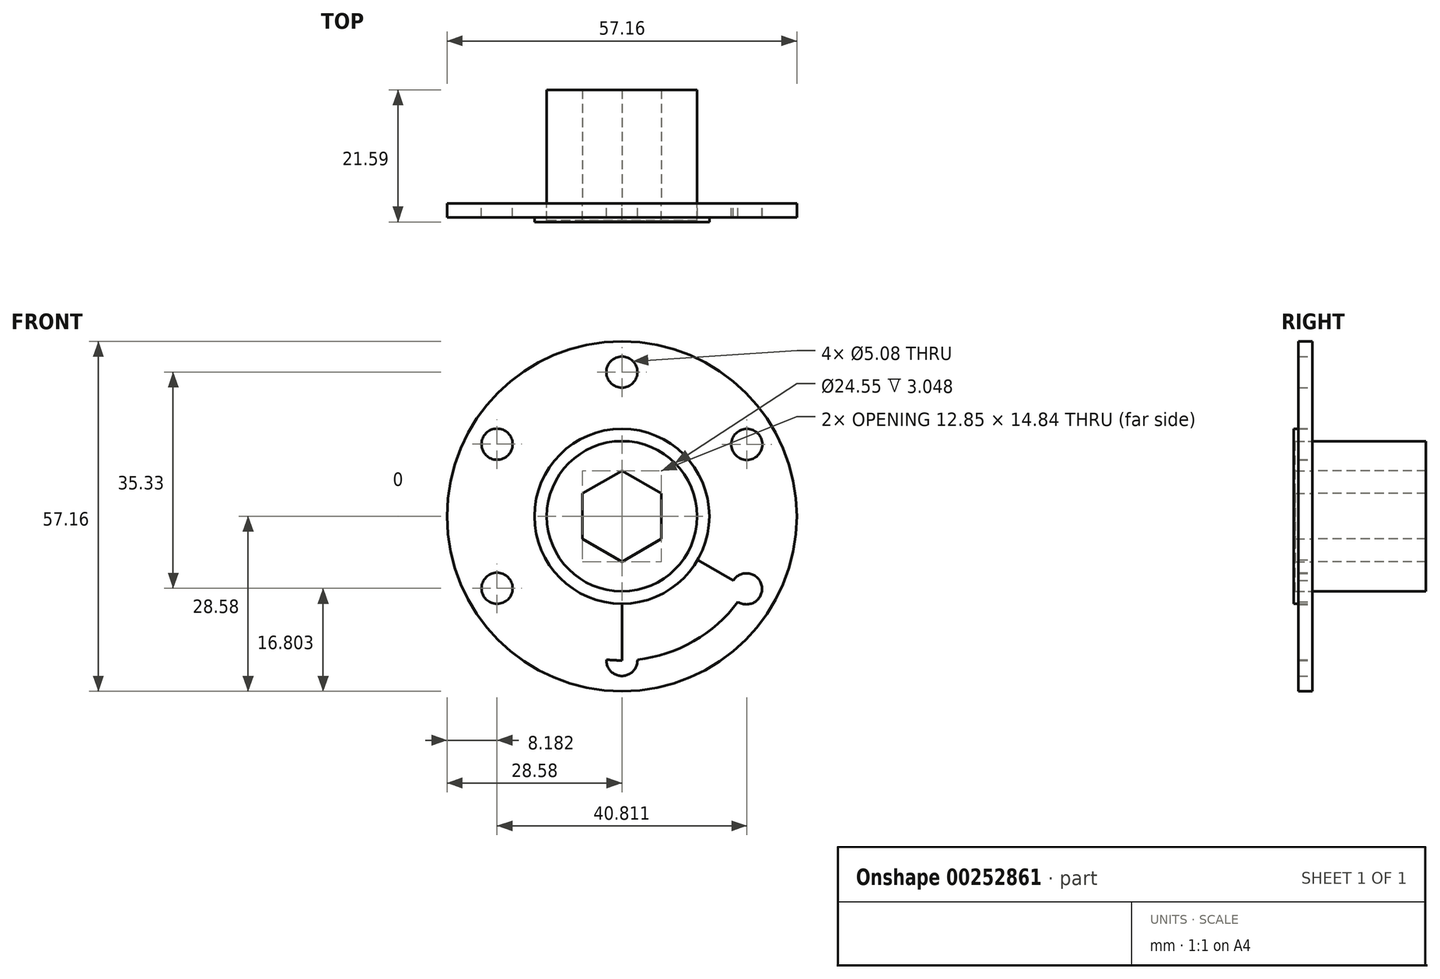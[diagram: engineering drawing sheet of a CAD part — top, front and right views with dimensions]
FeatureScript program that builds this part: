
annotation { "Feature Type Name" : "Feature", "Feature Type Description" : "" }
export const myFeature = defineFeature(function(context is Context, id is Id, definition is map)
    precondition{}
    {
        {
            var Q0;
            Q0=qCreatedBy(makeId("Front.planeOp"),FACE);
            var sketch = newSketch(context, id + "F0", { "sketchPlane" : qUnion([Q0])});
            skCircle(sketch, "E0", {"center": v(0, 0) * mm, "radius": 28.58 * mm});
            skPoint(sketch, "E1", {"position": v(0, 28.58) * mm});
            skPoint(sketch, "E2", {"position": v(0, -28.58) * mm});
            skLineSegment(sketch, "E3", {"start": v(0, 0) * mm, "end": v(-47.7, 27.54) * mm});
            skLineSegment(sketch, "E4.MirrorCS", {"start": v(0, 0) * mm, "end": v(-47.7, -27.54) * mm});
            skCircle(sketch, "E5.cCircle", {"center": v(0, 0) * mm, "radius": 6.43 * mm, "construction": true});
            skLineSegment(sketch, "E5.0", {"start": v(0, 7.42) * mm, "end": v(6.43, 3.71) * mm});
            skLineSegment(sketch, "E5.1", {"start": v(6.43, 3.71) * mm, "end": v(6.43, -3.71) * mm});
            skLineSegment(sketch, "E5.2", {"start": v(6.43, -3.71) * mm, "end": v(0, -7.42) * mm});
            skLineSegment(sketch, "E5.3", {"start": v(0, -7.42) * mm, "end": v(-6.43, -3.71) * mm});
            skLineSegment(sketch, "E5.4", {"start": v(-6.43, -3.71) * mm, "end": v(-6.43, 3.71) * mm});
            skLineSegment(sketch, "E5.5", {"start": v(-6.43, 3.71) * mm, "end": v(0, 7.42) * mm});
            skPoint(sketch, "E5.0.midPoint", {"position": v(3.21, 5.57) * mm});
            skCircle(sketch, "E6", {"center": v(0, 0) * mm, "radius": 23.55 * mm});
            skCircle(sketch, "E7", {"center": v(-20.4, 11.78) * mm, "radius": 2.54 * mm});
            skCircle(sketch, "E8", {"center": v(-20.4, -11.78) * mm, "radius": 2.54 * mm});
            skCircle(sketch, "E9", {"center": v(0, -23.55) * mm, "radius": 2.54 * mm});
            skCircle(sketch, "E10", {"center": v(0, 23.55) * mm, "radius": 2.54 * mm});
            skCircle(sketch, "E11", {"center": v(20.41, 11.75) * mm, "radius": 2.54 * mm});
            skCircle(sketch, "E12", {"center": v(20.35, -11.86) * mm, "radius": 2.54 * mm});
            skLineSegment(sketch, "E13", {"start": v(5.87, -2.62) * mm, "end": v(7.25, -3.23) * mm});
            skCircle(sketch, "E14", {"center": v(0, 0) * mm, "radius": 12.27 * mm});
            skCircle(sketch, "E15", {"center": v(0, 0) * mm, "radius": 14.29 * mm});
            skLineSegment(sketch, "E16.trimOffspring", {"start": v(21.26, -9.48) * mm, "end": v(21.5, -9.6) * mm});
            skLineSegment(sketch, "E17.MirrorCS", {"start": v(0, 0) * mm, "end": v(0, -55.09) * mm});
            skLineSegment(sketch, "E18.MirrorCS", {"start": v(0, 0) * mm, "end": v(0, 55.09) * mm});
            skLineSegment(sketch, "E19.MirrorCS", {"start": v(0, 0) * mm, "end": v(47.7, 27.54) * mm});
            skLineSegment(sketch, "E20.MirrorCS", {"start": v(0, 0) * mm, "end": v(47.7, -27.54) * mm});
            skPoint(sketch, "E21", {"position": v(0, 14.29) * mm});
            skPoint(sketch, "E22", {"position": v(0, -14.29) * mm});
            skSolve(sketch);
        }
        {
            var Q0;
            {var subQ0=sQuery(id+"F0.wireOp",EDGE,"E5.2");Q0=makeQuery(id+"F0.imprint","IMPRINT",FACE,{"disambiguationData":[TD([[makeQuery(id+"F0.imprint","IMPRINT",EDGE,{"derivedFrom":subQ0}),1.0]])]});}
            var Q1;
            {var subQ0=sQuery(id+"F0.wireOp",EDGE,"E5.3");Q1=makeQuery(id+"F0.imprint","IMPRINT",FACE,{"disambiguationData":[TD([[makeQuery(id+"F0.imprint","IMPRINT",EDGE,{"derivedFrom":subQ0}),1.0]])]});}
            var Q2;
            {var subQ0=sQuery(id+"F0.wireOp",EDGE,"E5.4");Q2=makeQuery(id+"F0.imprint","IMPRINT",FACE,{"disambiguationData":[TD([[makeQuery(id+"F0.imprint","IMPRINT",EDGE,{"derivedFrom":subQ0}),1.0]])]});}
            var Q3;
            {var subQ0=sQuery(id+"F0.wireOp",EDGE,"E5.5");Q3=makeQuery(id+"F0.imprint","IMPRINT",FACE,{"disambiguationData":[TD([[makeQuery(id+"F0.imprint","IMPRINT",EDGE,{"derivedFrom":subQ0}),1.0]])]});}
            var Q4;
            {var subQ0=sQuery(id+"F0.wireOp",EDGE,"E5.0");Q4=makeQuery(id+"F0.imprint","IMPRINT",FACE,{"disambiguationData":[TD([[makeQuery(id+"F0.imprint","IMPRINT",EDGE,{"derivedFrom":subQ0}),1.0]])]});}
            var Q5;
            {var subQ1=sQuery(id+"F0.wireOp",EDGE,"E5.1");var subQ8=makeQuery(id+"F0.imprint","IMPRINT",VERTEX,{"derivedFrom":subQ1});Q5=makeQuery(id+"F0.imprint","IMPRINT",FACE,{"disambiguationData":[TD([[makeQuery(id+"F0.imprint","IMPRINT",EDGE,{"disambiguationData":[TD([[subQ8,1.0]])],"derivedFrom":subQ1}),1.0]])]});}
            extrude(context, id + "F1", {"entities" : qUnion([Q0, Q1, Q2, Q3, Q4, Q5]), "oppositeDirection" : true, "depth" : 18.54 * mm});
        }
        {
            var Q0;
            {var subQ0=sQuery(id+"F0.wireOp",EDGE,"E17.MirrorCS");var subQ1=sQuery(id+"F0.wireOp",EDGE,"E14");var subQ2=makeQuery(id+"F0.imprint","INTERSECT",VERTEX,{"derivedFrom":[subQ1,subQ0]});Q0=makeQuery(id+"F0.imprint","IMPRINT",FACE,{"disambiguationData":[TD([[makeQuery(id+"F0.imprint","IMPRINT",EDGE,{"disambiguationData":[TD([[subQ2,-1.0]])],"derivedFrom":subQ1}),-1.0]])]});}
            var Q1;
            {var subQ0=sQuery(id+"F0.wireOp",EDGE,"E4.MirrorCS");var subQ1=sQuery(id+"F0.wireOp",EDGE,"E14");var subQ2=makeQuery(id+"F0.imprint","INTERSECT",VERTEX,{"derivedFrom":[subQ1,subQ0]});Q1=makeQuery(id+"F0.imprint","IMPRINT",FACE,{"disambiguationData":[TD([[makeQuery(id+"F0.imprint","IMPRINT",EDGE,{"disambiguationData":[TD([[subQ2,-1.0]])],"derivedFrom":subQ1}),-1.0]])]});}
            var Q2;
            {var subQ0=sQuery(id+"F0.wireOp",EDGE,"E14");var subQ1=sQuery(id+"F0.wireOp",EDGE,"E3");var subQ2=makeQuery(id+"F0.imprint","INTERSECT",VERTEX,{"derivedFrom":[subQ1,subQ0]});Q2=makeQuery(id+"F0.imprint","IMPRINT",FACE,{"disambiguationData":[TD([[makeQuery(id+"F0.imprint","IMPRINT",EDGE,{"disambiguationData":[TD([[subQ2,-1.0]])],"derivedFrom":subQ1}),1.0]])]});}
            var Q3;
            {var subQ0=sQuery(id+"F0.wireOp",EDGE,"E14");var subQ1=sQuery(id+"F0.wireOp",EDGE,"E3");var subQ2=makeQuery(id+"F0.imprint","INTERSECT",VERTEX,{"derivedFrom":[subQ1,subQ0]});Q3=makeQuery(id+"F0.imprint","IMPRINT",FACE,{"disambiguationData":[TD([[makeQuery(id+"F0.imprint","IMPRINT",EDGE,{"disambiguationData":[TD([[subQ2,-1.0]])],"derivedFrom":subQ1}),-1.0]])]});}
            var Q4;
            {var subQ0=sQuery(id+"F0.wireOp",EDGE,"E18.MirrorCS");var subQ1=sQuery(id+"F0.wireOp",EDGE,"E14");var subQ2=makeQuery(id+"F0.imprint","INTERSECT",VERTEX,{"derivedFrom":[subQ1,subQ0]});Q4=makeQuery(id+"F0.imprint","IMPRINT",FACE,{"disambiguationData":[TD([[makeQuery(id+"F0.imprint","IMPRINT",EDGE,{"disambiguationData":[TD([[subQ2,1.0]])],"derivedFrom":subQ1}),-1.0]])]});}
            var Q5;
            {var subQ0=sQuery(id+"F0.wireOp",EDGE,"E19.MirrorCS");var subQ1=sQuery(id+"F0.wireOp",EDGE,"E14");var subQ2=makeQuery(id+"F0.imprint","INTERSECT",VERTEX,{"derivedFrom":[subQ1,subQ0]});Q5=makeQuery(id+"F0.imprint","IMPRINT",FACE,{"disambiguationData":[TD([[makeQuery(id+"F0.imprint","IMPRINT",EDGE,{"disambiguationData":[TD([[subQ2,1.0]])],"derivedFrom":subQ1}),-1.0]])]});}
            extrude(context, id + "F2", {"entities" : qUnion([Q0, Q1, Q2, Q3, Q4, Q5]), "operationType" : NewBodyOperationType.ADD, "depth" : 3.05 * mm});
        }
        {
            var Q0;
            {var subQ6=sQuery(id+"F0.wireOp",EDGE,"E6");var subQ9=sQuery(id+"F0.wireOp",EDGE,"E9");var subQ10=makeQuery(id+"F0.imprint","INTERSECT",VERTEX,{"disambiguationData":[OD(1.0)],"derivedFrom":[subQ6,subQ9]});Q0=makeQuery(id+"F0.imprint","IMPRINT",FACE,{"disambiguationData":[TD([[makeQuery(id+"F0.imprint","IMPRINT",EDGE,{"disambiguationData":[TD([[subQ10,-1.0]])],"derivedFrom":subQ6}),1.0]])]});}
            var Q1;
            {var subQ5=sQuery(id+"F0.wireOp",EDGE,"E8");var subQ6=sQuery(id+"F0.wireOp",EDGE,"E6");var subQ7=makeQuery(id+"F0.imprint","INTERSECT",VERTEX,{"disambiguationData":[OD(1.0)],"derivedFrom":[subQ6,subQ5]});Q1=makeQuery(id+"F0.imprint","IMPRINT",FACE,{"disambiguationData":[TD([[makeQuery(id+"F0.imprint","IMPRINT",EDGE,{"disambiguationData":[TD([[subQ7,-1.0]])],"derivedFrom":subQ6}),1.0]])]});}
            var Q2;
            {var subQ7=sQuery(id+"F0.wireOp",EDGE,"E3");var subQ9=sQuery(id+"F0.wireOp",EDGE,"E15");var subQ10=makeQuery(id+"F0.imprint","INTERSECT",VERTEX,{"derivedFrom":[subQ7,subQ9]});Q2=makeQuery(id+"F0.imprint","IMPRINT",FACE,{"disambiguationData":[TD([[makeQuery(id+"F0.imprint","IMPRINT",EDGE,{"disambiguationData":[TD([[subQ10,-1.0]])],"derivedFrom":subQ7}),1.0]])]});}
            var Q3;
            {var subQ6=sQuery(id+"F0.wireOp",EDGE,"E3");var subQ9=sQuery(id+"F0.wireOp",EDGE,"E15");var subQ11=makeQuery(id+"F0.imprint","INTERSECT",VERTEX,{"derivedFrom":[subQ6,subQ9]});Q3=makeQuery(id+"F0.imprint","IMPRINT",FACE,{"disambiguationData":[TD([[makeQuery(id+"F0.imprint","IMPRINT",EDGE,{"disambiguationData":[TD([[subQ11,-1.0]])],"derivedFrom":subQ6}),-1.0]])]});}
            var Q4;
            {var subQ5=sQuery(id+"F0.wireOp",EDGE,"E11");var subQ7=sQuery(id+"F0.wireOp",EDGE,"E6");var subQ8=makeQuery(id+"F0.imprint","INTERSECT",VERTEX,{"disambiguationData":[OD(1.0)],"derivedFrom":[subQ7,subQ5]});Q4=makeQuery(id+"F0.imprint","IMPRINT",FACE,{"disambiguationData":[TD([[makeQuery(id+"F0.imprint","IMPRINT",EDGE,{"disambiguationData":[TD([[subQ8,-1.0]])],"derivedFrom":subQ7}),1.0]])]});}
            var Q5;
            {var subQ5=sQuery(id+"F0.wireOp",EDGE,"E6");var subQ9=sQuery(id+"F0.wireOp",EDGE,"E11");var subQ10=makeQuery(id+"F0.imprint","INTERSECT",VERTEX,{"disambiguationData":[OD(0.0)],"derivedFrom":[subQ5,subQ9]});Q5=makeQuery(id+"F0.imprint","IMPRINT",FACE,{"disambiguationData":[TD([[makeQuery(id+"F0.imprint","IMPRINT",EDGE,{"disambiguationData":[TD([[subQ10,1.0]])],"derivedFrom":subQ9}),-1.0]])]});}
            extrude(context, id + "F3", {"entities" : qUnion([Q0, Q1, Q2, Q3, Q4, Q5]), "operationType" : NewBodyOperationType.ADD, "depth" : 2.3 * mm});
        }
        {
            var Q0;
            {var subQ7=sQuery(id+"F0.wireOp",EDGE,"E18.MirrorCS");var subQ9=sQuery(id+"F0.wireOp",EDGE,"E0");var subQ10=makeQuery(id+"F0.imprint","INTERSECT",VERTEX,{"derivedFrom":[subQ9,subQ7]});Q0=makeQuery(id+"F0.imprint","IMPRINT",FACE,{"disambiguationData":[TD([[makeQuery(id+"F0.imprint","IMPRINT",EDGE,{"disambiguationData":[TD([[subQ10,1.0]])],"derivedFrom":subQ9}),1.0]])]});}
            var Q1;
            {var subQ6=sQuery(id+"F0.wireOp",EDGE,"E0");var subQ9=sQuery(id+"F0.wireOp",EDGE,"E18.MirrorCS");var subQ10=makeQuery(id+"F0.imprint","INTERSECT",VERTEX,{"derivedFrom":[subQ6,subQ9]});Q1=makeQuery(id+"F0.imprint","IMPRINT",FACE,{"disambiguationData":[TD([[makeQuery(id+"F0.imprint","IMPRINT",EDGE,{"disambiguationData":[TD([[subQ10,-1.0]])],"derivedFrom":subQ6}),1.0]])]});}
            var Q2;
            {var subQ5=sQuery(id+"F0.wireOp",EDGE,"E3");var subQ6=sQuery(id+"F0.wireOp",EDGE,"E0");var subQ7=makeQuery(id+"F0.imprint","INTERSECT",VERTEX,{"derivedFrom":[subQ6,subQ5]});Q2=makeQuery(id+"F0.imprint","IMPRINT",FACE,{"disambiguationData":[TD([[makeQuery(id+"F0.imprint","IMPRINT",EDGE,{"disambiguationData":[TD([[subQ7,-1.0]])],"derivedFrom":subQ6}),1.0]])]});}
            var Q3;
            {var subQ3=sQuery(id+"F0.wireOp",EDGE,"E4.MirrorCS");var subQ9=sQuery(id+"F0.wireOp",EDGE,"E0");var subQ10=makeQuery(id+"F0.imprint","INTERSECT",VERTEX,{"derivedFrom":[subQ9,subQ3]});Q3=makeQuery(id+"F0.imprint","IMPRINT",FACE,{"disambiguationData":[TD([[makeQuery(id+"F0.imprint","IMPRINT",EDGE,{"disambiguationData":[TD([[subQ10,-1.0]])],"derivedFrom":subQ9}),1.0]])]});}
            var Q4;
            {var subQ7=sQuery(id+"F0.wireOp",EDGE,"E17.MirrorCS");var subQ9=sQuery(id+"F0.wireOp",EDGE,"E0");var subQ11=makeQuery(id+"F0.imprint","INTERSECT",VERTEX,{"derivedFrom":[subQ9,subQ7]});Q4=makeQuery(id+"F0.imprint","IMPRINT",FACE,{"disambiguationData":[TD([[makeQuery(id+"F0.imprint","IMPRINT",EDGE,{"disambiguationData":[TD([[subQ11,-1.0]])],"derivedFrom":subQ9}),1.0]])]});}
            var Q5;
            {var subQ7=sQuery(id+"F0.wireOp",EDGE,"E19.MirrorCS");var subQ9=sQuery(id+"F0.wireOp",EDGE,"E0");var subQ10=makeQuery(id+"F0.imprint","INTERSECT",VERTEX,{"derivedFrom":[subQ9,subQ7]});Q5=makeQuery(id+"F0.imprint","IMPRINT",FACE,{"disambiguationData":[TD([[makeQuery(id+"F0.imprint","IMPRINT",EDGE,{"disambiguationData":[TD([[subQ10,1.0]])],"derivedFrom":subQ9}),1.0]])]});}
            extrude(context, id + "F4", {"entities" : qUnion([Q0, Q1, Q2, Q3, Q4, Q5]), "depth" : 2.3 * mm});
        }
        {
            var Q0;
            Q0=makeQuery(id+"F4.opExtrude","SWEPT_BODY",BODY,{"disambiguationData":[OSD([sQuery(id+"F0.wireOp",EDGE,"E0"),sQuery(id+"F0.wireOp",EDGE,"E6"),sQuery(id+"F0.wireOp",EDGE,"E7"),sQuery(id+"F0.wireOp",EDGE,"E8"),sQuery(id+"F0.wireOp",EDGE,"E9"),sQuery(id+"F0.wireOp",EDGE,"E10"),sQuery(id+"F0.wireOp",EDGE,"E11"),sQuery(id+"F0.wireOp",EDGE,"E12")])]});
            var Q1;
            Q1=makeQuery(id+"F3.opExtrude","SWEPT_BODY",BODY,{"disambiguationData":[OSD([sQuery(id+"F0.wireOp",EDGE,"E6"),sQuery(id+"F0.wireOp",EDGE,"E7"),sQuery(id+"F0.wireOp",EDGE,"E8"),sQuery(id+"F0.wireOp",EDGE,"E9"),sQuery(id+"F0.wireOp",EDGE,"E10"),sQuery(id+"F0.wireOp",EDGE,"E11"),sQuery(id+"F0.wireOp",EDGE,"E12"),sQuery(id+"F0.wireOp",EDGE,"E15")])]});
            var Q2;
            Q2=makeQuery(id+"F2.opExtrude","SWEPT_BODY",BODY,{"disambiguationData":[OSD([sQuery(id+"F0.wireOp",EDGE,"E14"),sQuery(id+"F0.wireOp",EDGE,"E15")])]});
            var Q3;
            Q3=makeQuery(id+"F1.opExtrude","SWEPT_BODY",BODY,{"disambiguationData":[OSD([sQuery(id+"F0.wireOp",EDGE,"E5.0"),sQuery(id+"F0.wireOp",EDGE,"E5.1"),sQuery(id+"F0.wireOp",EDGE,"E5.2"),sQuery(id+"F0.wireOp",EDGE,"E5.3"),sQuery(id+"F0.wireOp",EDGE,"E5.4"),sQuery(id+"F0.wireOp",EDGE,"E5.5"),sQuery(id+"F0.wireOp",EDGE,"E14")])]});
            booleanBodies(context, id + "F5", {"operationType" : BooleanOperationType.UNION, "tools" : qUnion([Q0, Q1, Q2, Q3])});
        }
        {
            var Q0;
            {var subQ0=sQuery(id+"F0.wireOp",EDGE,"E5.0");Q0=makeQuery(id+"F0.imprint","IMPRINT",FACE,{"disambiguationData":[TD([[makeQuery(id+"F0.imprint","IMPRINT",EDGE,{"derivedFrom":subQ0}),1.0]])]});}
            var Q1;
            {var subQ0=sQuery(id+"F0.wireOp",EDGE,"E5.5");Q1=makeQuery(id+"F0.imprint","IMPRINT",FACE,{"disambiguationData":[TD([[makeQuery(id+"F0.imprint","IMPRINT",EDGE,{"derivedFrom":subQ0}),1.0]])]});}
            var Q2;
            {var subQ0=sQuery(id+"F0.wireOp",EDGE,"E5.4");Q2=makeQuery(id+"F0.imprint","IMPRINT",FACE,{"disambiguationData":[TD([[makeQuery(id+"F0.imprint","IMPRINT",EDGE,{"derivedFrom":subQ0}),1.0]])]});}
            var Q3;
            {var subQ0=sQuery(id+"F0.wireOp",EDGE,"E5.3");Q3=makeQuery(id+"F0.imprint","IMPRINT",FACE,{"disambiguationData":[TD([[makeQuery(id+"F0.imprint","IMPRINT",EDGE,{"derivedFrom":subQ0}),1.0]])]});}
            var Q4;
            {var subQ0=sQuery(id+"F0.wireOp",EDGE,"E5.2");Q4=makeQuery(id+"F0.imprint","IMPRINT",FACE,{"disambiguationData":[TD([[makeQuery(id+"F0.imprint","IMPRINT",EDGE,{"derivedFrom":subQ0}),1.0]])]});}
            var Q5;
            {var subQ1=sQuery(id+"F0.wireOp",EDGE,"E5.1");var subQ8=makeQuery(id+"F0.imprint","IMPRINT",VERTEX,{"derivedFrom":subQ1});Q5=makeQuery(id+"F0.imprint","IMPRINT",FACE,{"disambiguationData":[TD([[makeQuery(id+"F0.imprint","IMPRINT",EDGE,{"disambiguationData":[TD([[subQ8,1.0]])],"derivedFrom":subQ1}),1.0]])]});}
            extrude(context, id + "F6", {"entities" : qUnion([Q0, Q1, Q2, Q3, Q4, Q5]), "depth" : 2.8 * mm});
        }
    });
